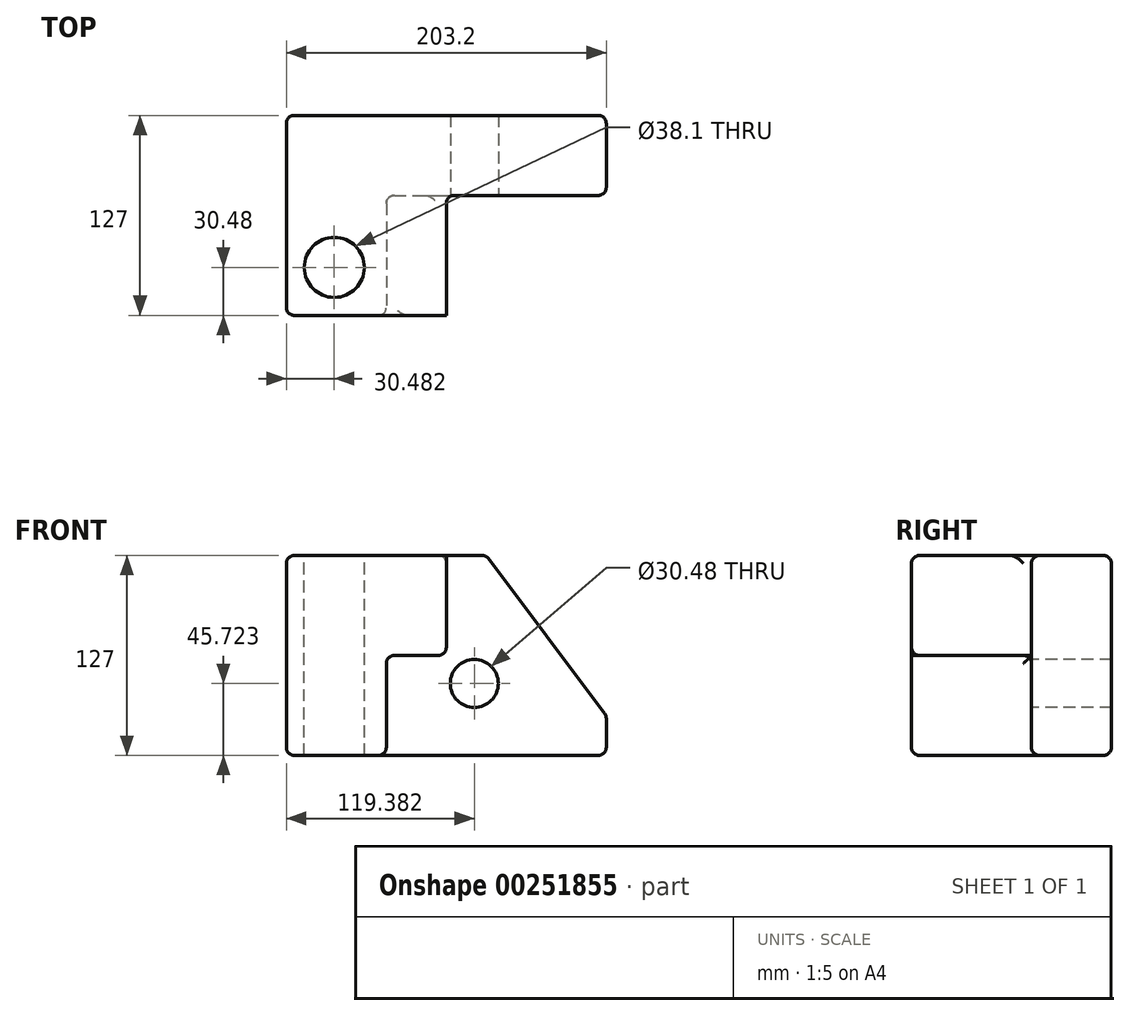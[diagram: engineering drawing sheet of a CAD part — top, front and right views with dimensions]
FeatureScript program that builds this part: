
annotation { "Feature Type Name" : "Feature", "Feature Type Description" : "" }
export const myFeature = defineFeature(function(context is Context, id is Id, definition is map)
    precondition{}
    {
        {
            var Q0;
            Q0=qCreatedBy(makeId("Front.planeOp"),FACE);
            var sketch = newSketch(context, id + "F0", { "sketchPlane" : qUnion([Q0])});
            skLineSegment(sketch, "E0", {"start": v(-71.3, 67.15) * mm, "end": v(-71.3, -59.85) * mm});
            skLineSegment(sketch, "E1", {"start": v(-71.3, -59.85) * mm, "end": v(131.9, -59.85) * mm});
            skLineSegment(sketch, "E2", {"start": v(-71.3, 67.15) * mm, "end": v(131.9, 67.15) * mm});
            skLineSegment(sketch, "E3", {"start": v(131.9, 67.15) * mm, "end": v(131.9, -59.85) * mm});
            skSolve(sketch);
        }
        {
            var Q0;
            Q0=makeQuery(id+"F0.imprint","IMPRINT",FACE,{"disambiguationData":[TD([[makeQuery(id+"F0.imprint","IMPRINT",EDGE,{"derivedFrom":sQuery(id+"F0.wireOp",EDGE,"E0")}),1.0]])]});
            extrude(context, id + "F1", {"entities" : qUnion([Q0]), "depth" : 127 * mm});
        }
        {
            var Q0;
            Q0=makeQuery(id+"F1.opExtrude","CAP_FACE",FACE,{"disambiguationData":[OSD([sQuery(id+"F0.wireOp",EDGE,"E0"),sQuery(id+"F0.wireOp",EDGE,"E1"),sQuery(id+"F0.wireOp",EDGE,"E2"),sQuery(id+"F0.wireOp",EDGE,"E3")])],"isStart":false});
            var sketch = newSketch(context, id + "F2", { "sketchPlane" : qUnion([Q0])});
            skLineSegment(sketch, "E4", {"start": v(-71.3, -59.85) * mm, "end": v(-71.3, 67.15) * mm});
            skLineSegment(sketch, "E5", {"start": v(-71.3, 67.15) * mm, "end": v(30.3, 67.15) * mm});
            skLineSegment(sketch, "E6", {"start": v(-71.3, -59.85) * mm, "end": v(-7.8, -59.85) * mm});
            skLineSegment(sketch, "E7", {"start": v(-7.8, -59.85) * mm, "end": v(-7.8, 3.65) * mm});
            skLineSegment(sketch, "E8", {"start": v(-7.8, 3.65) * mm, "end": v(30.3, 3.65) * mm});
            skLineSegment(sketch, "E9", {"start": v(30.3, 3.65) * mm, "end": v(30.3, 67.15) * mm});
            skSolve(sketch);
        }
        {
            var Q0;
            {var subQ2=sQuery(id+"F2.wireOp",EDGE,"E7");Q0=makeQuery(id+"F2.imprint","IMPRINT",FACE,{"disambiguationData":[TD([[makeQuery(id+"F2.imprint","IMPRINT",EDGE,{"derivedFrom":subQ2}),-1.0]])]});}
            extrude(context, id + "F3", {"entities" : qUnion([Q0]), "operationType" : NewBodyOperationType.REMOVE, "oppositeDirection" : true, "depth" : 76.2 * mm});
        }
        {
            var Q0;
            Q0=makeQuery(id+"F1.opExtrude","SWEPT_EDGE",EDGE,{"disambiguationData":[OSD([sQuery(id+"F0.wireOp",EDGE,"E2"),sQuery(id+"F0.wireOp",EDGE,"E3")])]});
            chamfer(context, id + "F4", {"entities" : qUnion([Q0]), "chamferType" : ChamferType.TWO_OFFSETS, "width1" : 76.2 * mm, "oppositeDirection" : false, "width2" : 101.6 * mm, "tangentPropagation" : true});
        }
        {
            var Q0;
            Q0=makeQuery(id+"F3.opExtrude","SWEPT_EDGE",EDGE,{"disambiguationData":[OSD([sQuery(id+"F0.wireOp",EDGE,"E2"),sQuery(id+"F2.wireOp",EDGE,"E5"),sQuery(id+"F2.wireOp",EDGE,"E9")])]});
            var Q1;
            Q1=makeQuery(id+"F1.opExtrude","CAP_EDGE",EDGE,{"disambiguationData":[OSD([sQuery(id+"F0.wireOp",EDGE,"E2")])],"isStart":false});
            var Q2;
            {var subQ0=sQuery(id+"F0.wireOp",EDGE,"E2");Q2=makeQuery(id+"F4.opChamfer","BLEND_EDGE",EDGE,{"blendedFrom":[makeQuery(id+"F1.opExtrude","SWEPT_EDGE",EDGE,{"disambiguationData":[OSD([subQ0,sQuery(id+"F0.wireOp",EDGE,"E3")])]}),makeQuery(id+"F3.boolean.opBoolean","MERGE",FACE,{"derivedFrom":[makeQuery(id+"F1.opExtrude","SWEPT_FACE",FACE,{"disambiguationData":[OSD([subQ0])]}),makeQuery(id+"F3.opExtrude","SWEPT_FACE",FACE,{"disambiguationData":[OSD([sQuery(id+"F2.wireOp",EDGE,"E5")])]})]})],"blendedInto":[makeQuery(id+"F3.boolean.opBoolean","MERGE",FACE,{"derivedFrom":[makeQuery(id+"F1.opExtrude","SWEPT_FACE",FACE,{"disambiguationData":[OSD([subQ0])]}),makeQuery(id+"F3.opExtrude","SWEPT_FACE",FACE,{"disambiguationData":[OSD([sQuery(id+"F2.wireOp",EDGE,"E5")])]})]})]});}
            var Q3;
            {var subQ0=sQuery(id+"F0.wireOp",EDGE,"E3");Q3=makeQuery(id+"F4.opChamfer","BLEND_EDGE",EDGE,{"blendedFrom":[makeQuery(id+"F1.opExtrude","SWEPT_EDGE",EDGE,{"disambiguationData":[OSD([sQuery(id+"F0.wireOp",EDGE,"E2"),subQ0])]}),makeQuery(id+"F1.opExtrude","SWEPT_FACE",FACE,{"disambiguationData":[OSD([subQ0])]})],"blendedInto":[makeQuery(id+"F1.opExtrude","SWEPT_FACE",FACE,{"disambiguationData":[OSD([subQ0])]})]});}
            var Q4;
            Q4=makeQuery(id+"F1.opExtrude","SWEPT_EDGE",EDGE,{"disambiguationData":[OSD([sQuery(id+"F0.wireOp",EDGE,"E1"),sQuery(id+"F0.wireOp",EDGE,"E3")])]});
            var Q5;
            Q5=makeQuery(id+"F1.opExtrude","CAP_EDGE",EDGE,{"disambiguationData":[OSD([sQuery(id+"F0.wireOp",EDGE,"E1")])],"isStart":false});
            var Q6;
            Q6=makeQuery(id+"F3.opExtrude","SWEPT_EDGE",EDGE,{"disambiguationData":[OSD([sQuery(id+"F0.wireOp",EDGE,"E1"),sQuery(id+"F2.wireOp",EDGE,"E6"),sQuery(id+"F2.wireOp",EDGE,"E7")])]});
            var Q7;
            Q7=makeQuery(id+"F3.opExtrude","CAP_EDGE",EDGE,{"disambiguationData":[OSD([sQuery(id+"F2.wireOp",EDGE,"E7")])],"isStart":true});
            var Q8;
            Q8=makeQuery(id+"F3.opExtrude","SWEPT_EDGE",EDGE,{"disambiguationData":[OSD([sQuery(id+"F2.wireOp",EDGE,"E8"),sQuery(id+"F2.wireOp",EDGE,"E9")])]});
            var Q9;
            Q9=makeQuery(id+"F3.opExtrude","CAP_EDGE",EDGE,{"disambiguationData":[OSD([sQuery(id+"F2.wireOp",EDGE,"E9")])],"isStart":true});
            var Q10;
            Q10=makeQuery(id+"F3.opExtrude","CAP_EDGE",EDGE,{"disambiguationData":[OSD([sQuery(id+"F2.wireOp",EDGE,"E9")])],"isStart":false});
            var Q11;
            Q11=makeQuery(id+"F3.opExtrude","CAP_EDGE",EDGE,{"disambiguationData":[OSD([sQuery(id+"F2.wireOp",EDGE,"E8")])],"isStart":false});
            var Q12;
            Q12=makeQuery(id+"F3.opExtrude","CAP_EDGE",EDGE,{"disambiguationData":[OSD([sQuery(id+"F2.wireOp",EDGE,"E7")])],"isStart":false});
            var Q13;
            Q13=makeQuery(id+"F3.opExtrude","CAP_EDGE",EDGE,{"disambiguationData":[OSD([sQuery(id+"F2.wireOp",EDGE,"E6")])],"isStart":false});
            var Q14;
            Q14=makeQuery(id+"F3.opExtrude","CAP_EDGE",EDGE,{"disambiguationData":[OSD([sQuery(id+"F2.wireOp",EDGE,"E4")])],"isStart":false});
            var Q15;
            Q15=makeQuery(id+"F3.opExtrude","CAP_EDGE",EDGE,{"disambiguationData":[OSD([sQuery(id+"F2.wireOp",EDGE,"E5")])],"isStart":false});
            var Q16;
            {var subQ0=sQuery(id+"F0.wireOp",EDGE,"E3");var subQ1=sQuery(id+"F0.wireOp",EDGE,"E2");Q16=makeQuery(id+"F4.opChamfer","BLEND_EDGE",EDGE,{"blendedFrom":[makeQuery(id+"F1.opExtrude","SWEPT_EDGE",EDGE,{"disambiguationData":[OSD([subQ1,subQ0])]}),makeQuery(id+"F1.opExtrude","CAP_FACE",FACE,{"disambiguationData":[OSD([sQuery(id+"F0.wireOp",EDGE,"E0"),sQuery(id+"F0.wireOp",EDGE,"E1"),subQ1,subQ0])],"isStart":true})],"blendedInto":[makeQuery(id+"F1.opExtrude","CAP_FACE",FACE,{"disambiguationData":[OSD([sQuery(id+"F0.wireOp",EDGE,"E0"),sQuery(id+"F0.wireOp",EDGE,"E1"),subQ1,subQ0])],"isStart":true})]});}
            var Q17;
            {var subQ0=sQuery(id+"F0.wireOp",EDGE,"E3");var subQ1=sQuery(id+"F0.wireOp",EDGE,"E2");Q17=makeQuery(id+"F4.opChamfer","BLEND_EDGE",EDGE,{"blendedFrom":[makeQuery(id+"F1.opExtrude","SWEPT_EDGE",EDGE,{"disambiguationData":[OSD([subQ1,subQ0])]}),makeQuery(id+"F1.opExtrude","CAP_FACE",FACE,{"disambiguationData":[OSD([sQuery(id+"F0.wireOp",EDGE,"E0"),sQuery(id+"F0.wireOp",EDGE,"E1"),subQ1,subQ0])],"isStart":false})],"blendedInto":[makeQuery(id+"F1.opExtrude","CAP_FACE",FACE,{"disambiguationData":[OSD([sQuery(id+"F0.wireOp",EDGE,"E0"),sQuery(id+"F0.wireOp",EDGE,"E1"),subQ1,subQ0])],"isStart":false})]});}
            var Q18;
            Q18=makeQuery(id+"F1.opExtrude","CAP_EDGE",EDGE,{"disambiguationData":[OSD([sQuery(id+"F0.wireOp",EDGE,"E3")])],"isStart":false});
            var Q19;
            Q19=makeQuery(id+"F1.opExtrude","CAP_EDGE",EDGE,{"disambiguationData":[OSD([sQuery(id+"F0.wireOp",EDGE,"E3")])],"isStart":true});
            var Q20;
            Q20=makeQuery(id+"F1.opExtrude","CAP_EDGE",EDGE,{"disambiguationData":[OSD([sQuery(id+"F0.wireOp",EDGE,"E2")])],"isStart":true});
            var Q21;
            Q21=makeQuery(id+"F1.opExtrude","CAP_EDGE",EDGE,{"disambiguationData":[OSD([sQuery(id+"F0.wireOp",EDGE,"E1")])],"isStart":true});
            var Q22;
            Q22=makeQuery(id+"F1.opExtrude","CAP_EDGE",EDGE,{"disambiguationData":[OSD([sQuery(id+"F0.wireOp",EDGE,"E0")])],"isStart":true});
            var Q23;
            Q23=makeQuery(id+"F3.boolean.opBoolean","MERGE",EDGE,{"derivedFrom":[makeQuery(id+"F1.opExtrude","SWEPT_EDGE",EDGE,{"disambiguationData":[OSD([sQuery(id+"F0.wireOp",EDGE,"E0"),sQuery(id+"F0.wireOp",EDGE,"E2")])]}),makeQuery(id+"F3.opExtrude","SWEPT_EDGE",EDGE,{"disambiguationData":[OSD([sQuery(id+"F2.wireOp",EDGE,"E4"),sQuery(id+"F2.wireOp",EDGE,"E5")])]})]});
            var Q24;
            Q24=makeQuery(id+"F3.boolean.opBoolean","MERGE",EDGE,{"derivedFrom":[makeQuery(id+"F1.opExtrude","SWEPT_EDGE",EDGE,{"disambiguationData":[OSD([sQuery(id+"F0.wireOp",EDGE,"E0"),sQuery(id+"F0.wireOp",EDGE,"E1")])]}),makeQuery(id+"F3.opExtrude","SWEPT_EDGE",EDGE,{"disambiguationData":[OSD([sQuery(id+"F2.wireOp",EDGE,"E4"),sQuery(id+"F2.wireOp",EDGE,"E6")])]})]});
            fillet(context, id + "F5", {"entities" : qUnion([Q0, Q1, Q2, Q3, Q4, Q5, Q6, Q7, Q8, Q9, Q10, Q11, Q12, Q13, Q14, Q15, Q16, Q17, Q18, Q19, Q20, Q21, Q22, Q23, Q24]), "radius" : 5.08 * mm, "tangentPropagation" : true, "allowEdgeOverflow" : false});
        }
        {
            var Q0;
            Q0=makeQuery(id+"F3.boolean.opBoolean","COPY",EDGE,{"derivedFrom":makeQuery(id+"F3.opExtrude","SWEPT_EDGE",EDGE,{"disambiguationData":[OSD([sQuery(id+"F0.wireOp",EDGE,"E2"),sQuery(id+"F2.wireOp",EDGE,"E5"),sQuery(id+"F2.wireOp",EDGE,"E9")])]})});
            var Q1;
            Q1=makeQuery(id+"F3.boolean.opBoolean","COPY",EDGE,{"derivedFrom":makeQuery(id+"F3.opExtrude","SWEPT_EDGE",EDGE,{"disambiguationData":[OSD([sQuery(id+"F2.wireOp",EDGE,"E8"),sQuery(id+"F2.wireOp",EDGE,"E9")])]})});
            var Q2;
            Q2=makeQuery(id+"F3.boolean.opBoolean","COPY",EDGE,{"derivedFrom":makeQuery(id+"F3.opExtrude","CAP_EDGE",EDGE,{"disambiguationData":[OSD([sQuery(id+"F2.wireOp",EDGE,"E9")])],"isStart":false})});
            var Q3;
            {var subQ0=sQuery(id+"F0.wireOp",EDGE,"E3");var subQ1=sQuery(id+"F0.wireOp",EDGE,"E2");Q3=makeQuery(id+"F4.opChamfer","BLEND_EDGE",EDGE,{"blendedFrom":[makeQuery(id+"F1.opExtrude","SWEPT_EDGE",EDGE,{"disambiguationData":[OSD([subQ1,subQ0])]}),makeQuery(id+"F3.boolean.opBoolean","COPY",FACE,{"derivedFrom":makeQuery(id+"F3.opExtrude","CAP_FACE",FACE,{"disambiguationData":[OSD([sQuery(id+"F0.wireOp",EDGE,"E1"),subQ1,subQ0,sQuery(id+"F2.wireOp",EDGE,"E7"),sQuery(id+"F2.wireOp",EDGE,"E8"),sQuery(id+"F2.wireOp",EDGE,"E9")])],"isStart":false})})],"blendedInto":[makeQuery(id+"F3.boolean.opBoolean","COPY",FACE,{"derivedFrom":makeQuery(id+"F3.opExtrude","CAP_FACE",FACE,{"disambiguationData":[OSD([sQuery(id+"F0.wireOp",EDGE,"E1"),subQ1,subQ0,sQuery(id+"F2.wireOp",EDGE,"E7"),sQuery(id+"F2.wireOp",EDGE,"E8"),sQuery(id+"F2.wireOp",EDGE,"E9")])],"isStart":false})})]});}
            var Q4;
            Q4=makeQuery(id+"F3.boolean.opBoolean","COPY",FACE,{"derivedFrom":makeQuery(id+"F3.opExtrude","SWEPT_FACE",FACE,{"disambiguationData":[OSD([sQuery(id+"F2.wireOp",EDGE,"E7")])]})});
            var Q5;
            Q5=makeQuery(id+"F3.boolean.opBoolean","COPY",EDGE,{"derivedFrom":makeQuery(id+"F3.opExtrude","SWEPT_EDGE",EDGE,{"disambiguationData":[OSD([sQuery(id+"F0.wireOp",EDGE,"E1"),sQuery(id+"F2.wireOp",EDGE,"E6"),sQuery(id+"F2.wireOp",EDGE,"E7")])]})});
            var Q6;
            Q6=makeQuery(id+"F1.opExtrude","CAP_EDGE",EDGE,{"disambiguationData":[OSD([sQuery(id+"F0.wireOp",EDGE,"E0")])],"isStart":false});
            fillet(context, id + "F6", {"entities" : qUnion([Q0, Q1, Q2, Q3, Q4, Q5, Q6]), "radius" : 5.08 * mm, "tangentPropagation" : true, "allowEdgeOverflow" : false});
        }
        {
            var Q0;
            Q0=makeQuery(id+"F3.boolean.opBoolean","COPY",FACE,{"derivedFrom":makeQuery(id+"F3.opExtrude","CAP_FACE",FACE,{"disambiguationData":[OSD([sQuery(id+"F0.wireOp",EDGE,"E1"),sQuery(id+"F0.wireOp",EDGE,"E2"),sQuery(id+"F0.wireOp",EDGE,"E3"),sQuery(id+"F2.wireOp",EDGE,"E7"),sQuery(id+"F2.wireOp",EDGE,"E8"),sQuery(id+"F2.wireOp",EDGE,"E9")])],"isStart":false})});
            var sketch = newSketch(context, id + "F7", { "sketchPlane" : qUnion([Q0])});
            skCircle(sketch, "E10", {"center": v(48.08, -14.13) * mm, "radius": 15.24 * mm});
            skSolve(sketch);
        }
        {
            var Q0;
            Q0=makeQuery(id+"F7.imprint","IMPRINT",FACE,{"disambiguationData":[TD([[makeQuery(id+"F7.imprint","IMPRINT",EDGE,{"derivedFrom":sQuery(id+"F7.wireOp",EDGE,"E10")}),1.0]])]});
            var Q1;
            Q1=makeQuery(id+"F1.opExtrude","CAP_FACE",FACE,{"disambiguationData":[OSD([sQuery(id+"F0.wireOp",EDGE,"E0"),sQuery(id+"F0.wireOp",EDGE,"E1"),sQuery(id+"F0.wireOp",EDGE,"E2"),sQuery(id+"F0.wireOp",EDGE,"E3")])],"isStart":true});
            extrude(context, id + "F8", {"entities" : qUnion([Q0]), "operationType" : NewBodyOperationType.REMOVE, "endBound" : BoundingType.UP_TO_SURFACE, "oppositeDirection" : true, "endBoundEntityFace" : qUnion([Q1]), "depth" : 25.4 * mm});
        }
        {
            var Q0;
            Q0=makeQuery(id+"F1.opExtrude","SWEPT_FACE",FACE,{"disambiguationData":[OSD([sQuery(id+"F0.wireOp",EDGE,"E2")])]});
            var sketch = newSketch(context, id + "F9", { "sketchPlane" : qUnion([Q0])});
            skCircle(sketch, "E11", {"center": v(-40.82, -96.52) * mm, "radius": 19.05 * mm});
            skSolve(sketch);
        }
        {
            var Q0;
            Q0=makeQuery(id+"F9.imprint","IMPRINT",FACE,{"disambiguationData":[TD([[makeQuery(id+"F9.imprint","IMPRINT",EDGE,{"derivedFrom":sQuery(id+"F9.wireOp",EDGE,"E11")}),1.0]])]});
            var Q1;
            Q1=makeQuery(id+"F1.opExtrude","SWEPT_FACE",FACE,{"disambiguationData":[OSD([sQuery(id+"F0.wireOp",EDGE,"E1")])]});
            extrude(context, id + "F10", {"entities" : qUnion([Q0]), "operationType" : NewBodyOperationType.REMOVE, "endBound" : BoundingType.UP_TO_SURFACE, "oppositeDirection" : true, "endBoundEntityFace" : qUnion([Q1]), "depth" : 25.4 * mm});
        }
    });
